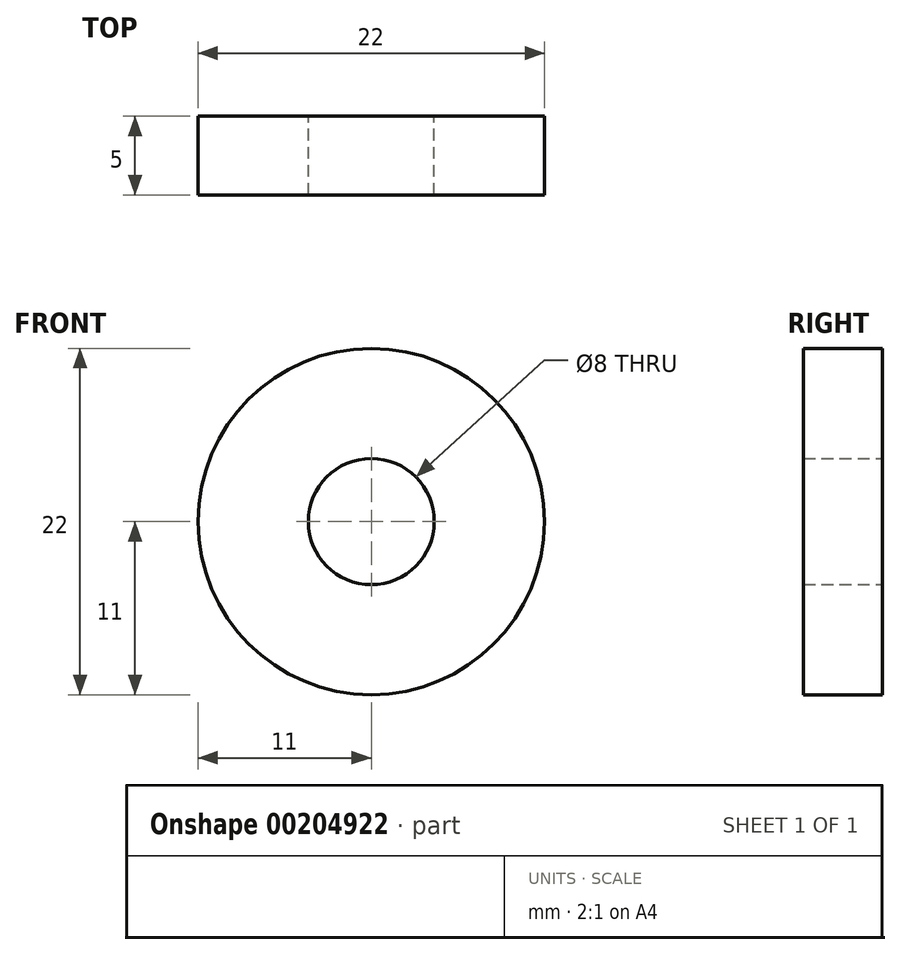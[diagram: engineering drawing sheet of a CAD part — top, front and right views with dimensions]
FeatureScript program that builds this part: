
annotation { "Feature Type Name" : "Feature", "Feature Type Description" : "" }
export const myFeature = defineFeature(function(context is Context, id is Id, definition is map)
    precondition{}
    {
        {
            var Q0;
            Q0=qCreatedBy(makeId("Front.planeOp"),FACE);
            var sketch = newSketch(context, id + "F0", { "sketchPlane" : qUnion([Q0])});
            skCircle(sketch, "E0", {"center": v(0, 0) * mm, "radius": 11 * mm});
            skCircle(sketch, "E1", {"center": v(0, 0) * mm, "radius": 4 * mm});
            skSolve(sketch);
        }
        {
            var Q0;
            Q0=makeQuery(id+"F0.imprint","IMPRINT",FACE,{"disambiguationData":[TD([[makeQuery(id+"F0.imprint","IMPRINT",EDGE,{"derivedFrom":sQuery(id+"F0.wireOp",EDGE,"E0")}),1.0]])]});
            extrude(context, id + "F1", {"entities" : qUnion([Q0]), "depth" : 5 * mm});
        }
    });
